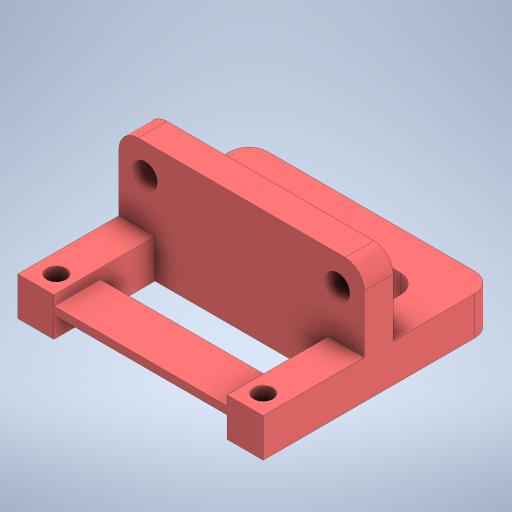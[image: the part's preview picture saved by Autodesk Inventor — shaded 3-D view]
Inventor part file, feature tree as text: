
AUTODESK INVENTOR PART (.ipt)
format: ipt  version: 2023 (Build 270158000, 158)  size: 390,656 bytes
history: native  units: mm
features: extrude x7, sketch x6, projected_geometry x3, other x2, fillet x2, chamfer x1
ambient origin geometry x8: Origin, YZ Plane, XZ Plane, XY Plane, X Axis, Y Axis, Z Axis, Center Point
bodies: Body1 (feature_tree)
feature tree (21):
  other  "솔리드1"
  sketch  "스케치1"
  extrude  "돌출1"  Depth=2.0mm
  extrude  "돌출2"  Depth=25.5mm
  fillet  "모깎기1"  Radius=24.0mm
  fillet  "모깎기4"  Radius=2.0mm
  other  "작업 평면1"
  extrude  "돌출5"  Depth=2.0mm
  chamfer  "모따기1"  Distance=18.0mm
  extrude  "돌출6"  Depth=20.0mm
  extrude  "돌출7"  Depth=5.0mm TaperAngle=0.0deg
  extrude  "돌출8"  Depth=10.0mm
  extrude  "돌출10"  Depth=10.5mm
  sketch  "스케치2"
  sketch  "스케치5"
  sketch  "스케치6"
  sketch  "스케치8"
  sketch  "스케치10"
  projected_geometry  "투영된 루프4"
  projected_geometry  "투영된 루프5"
  projected_geometry  "투영된 루프6"
